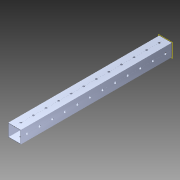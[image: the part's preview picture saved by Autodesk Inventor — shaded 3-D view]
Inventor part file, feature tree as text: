
AUTODESK INVENTOR PART (.ipt)
format: ipt  version: 2014 (Build 180170000, 170)  size: 1,172,480 bytes
history: native  units: in
note: dims shown in document units (in); Inventor stores cm internally (conversion verified against a paired STEP export)
features: pattern_circular x1, other x1, plane x1, extrude x1, imported_body x1, sketch x1
ambient origin geometry x8: Origin, YZ Plane, XZ Plane, XY Plane, X Axis, Y Axis, Z Axis, Center Point
bodies: Body1 (feature_tree)
feature tree (6):
  pattern_circular  "CirPattern2"
  other  "217-3426-STEP1"
  plane  "Work Plane1"
  extrude  "Extrusion1"  Depth=3937.0079in TaperAngle=0.0deg
  imported_body  "Base1"
  sketch  "Sketch1"  dims[d0=-12.0in d1=3937.0079in d2=0.0in]
